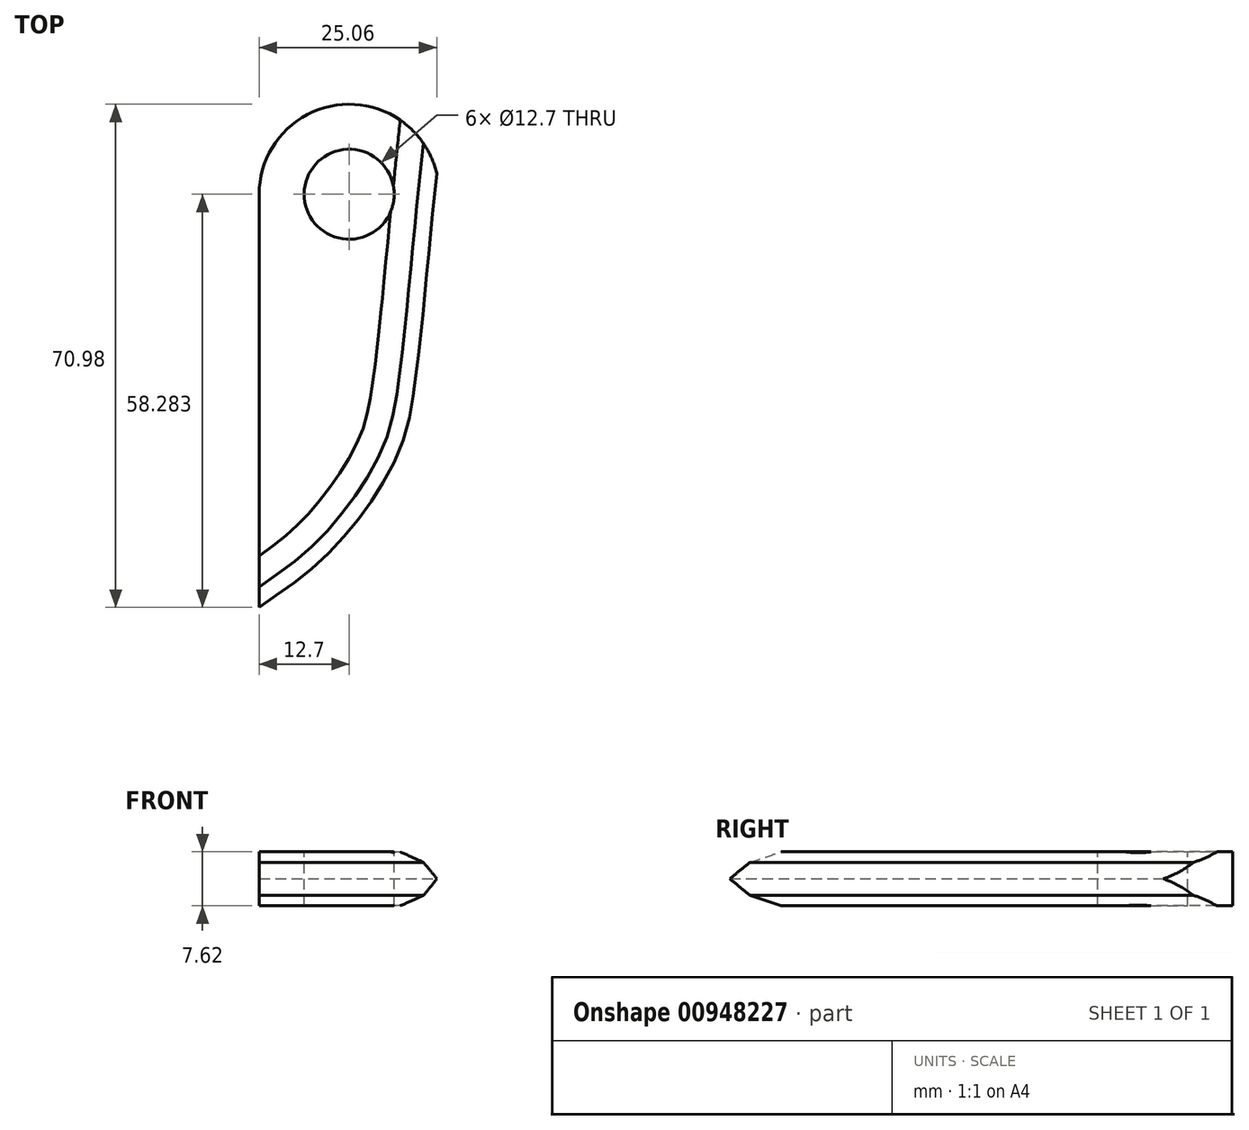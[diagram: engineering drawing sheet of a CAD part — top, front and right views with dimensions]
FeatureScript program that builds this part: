
annotation { "Feature Type Name" : "Feature", "Feature Type Description" : "" }
export const myFeature = defineFeature(function(context is Context, id is Id, definition is map)
    precondition{}
    {
        {
            var Q0;
            Q0=qCreatedBy(makeId("Top.planeOp"),FACE);
            var sketch = newSketch(context, id + "F0", { "sketchPlane" : qUnion([Q0])});
            skFitSpline(sketch, "E0", {"points": [v(-12.7, -23.04) * mm, v(-2.33, -14.95) * mm, v(6.74, -2.45) * mm, v(9.68, 7.6) * mm, v(12.7, 36.02) * mm], "startDerivative": vector(46.26, 33.05) * mm, "endDerivative": vector(9.99, 96.34) * mm});
            skLineSegment(sketch, "E1", {"start": v(-12.7, 36.02) * mm, "end": v(-12.7, -23.04) * mm});
            skArc(sketch, "E2", {"start": v(12.7, 36.02) * mm, "mid": v(0, 48.72) * mm, "end": v(-12.7, 36.02) * mm});
            skSolve(sketch);
        }
        {
            var Q0;
            Q0=makeQuery(id+"F0.imprint","IMPRINT",FACE,{"disambiguationData":[TD([[makeQuery(id+"F0.imprint","IMPRINT",EDGE,{"derivedFrom":sQuery(id+"F0.wireOp",EDGE,"E0")}),1.0]])]});
            extrude(context, id + "F1", {"entities" : qUnion([Q0]), "depth" : 7.62 * mm, "offsetDistance" : 25.4 * mm});
        }
        {
            var Q0;
            Q0=makeQuery(id+"F1.opExtrude","CAP_FACE",FACE,{"disambiguationData":[OSD([sQuery(id+"F0.wireOp",EDGE,"E0"),sQuery(id+"F0.wireOp",EDGE,"E1"),sQuery(id+"F0.wireOp",EDGE,"E2")])],"isStart":false});
            var sketch = newSketch(context, id + "F2", { "sketchPlane" : qUnion([Q0])});
            skCircle(sketch, "E3", {"center": v(0, 36.02) * mm, "radius": 6.35 * mm});
            skSolve(sketch);
        }
        {
            var Q0;
            Q0=makeQuery(id+"F2.imprint","IMPRINT",FACE,{"disambiguationData":[TD([[makeQuery(id+"F2.imprint","IMPRINT",EDGE,{"derivedFrom":sQuery(id+"F2.wireOp",EDGE,"E3")}),1.0]])]});
            extrude(context, id + "F3", {"entities" : qUnion([Q0]), "operationType" : NewBodyOperationType.REMOVE, "oppositeDirection" : true, "depth" : 25.4 * mm, "offsetDistance" : 25.4 * mm});
        }
        {
            var Q0;
            Q0=makeQuery(id+"F1.opExtrude","CAP_EDGE",EDGE,{"disambiguationData":[OSD([sQuery(id+"F0.wireOp",EDGE,"E0")])],"isStart":false});
            chamfer(context, id + "F4", {"entities" : qUnion([Q0]), "width" : 4.44 * mm, "tangentPropagation" : true});
        }
        {
            var Q0;
            Q0=makeQuery(id+"F1.opExtrude","CAP_EDGE",EDGE,{"disambiguationData":[OSD([sQuery(id+"F0.wireOp",EDGE,"E0")])],"isStart":true});
            chamfer(context, id + "F5", {"entities" : qUnion([Q0]), "width" : 4.44 * mm, "tangentPropagation" : true});
        }
        {
            var Q0;
            {var subQ0=sQuery(id+"F0.wireOp",EDGE,"E0");Q0=makeQuery(id+"F4.opChamfer","BLEND_EDGE",EDGE,{"blendedFrom":[makeQuery(id+"F1.opExtrude","CAP_EDGE",EDGE,{"disambiguationData":[OSD([subQ0])],"isStart":false}),makeQuery(id+"F1.opExtrude","CAP_FACE",FACE,{"disambiguationData":[OSD([subQ0,sQuery(id+"F0.wireOp",EDGE,"E1"),sQuery(id+"F0.wireOp",EDGE,"E2")])],"isStart":false})],"blendedInto":[makeQuery(id+"F1.opExtrude","CAP_FACE",FACE,{"disambiguationData":[OSD([subQ0,sQuery(id+"F0.wireOp",EDGE,"E1"),sQuery(id+"F0.wireOp",EDGE,"E2")])],"isStart":false})]});}
            chamfer(context, id + "F6", {"entities" : qUnion([Q0]), "width" : 5.08 * mm, "tangentPropagation" : true});
        }
        {
            var Q0;
            {var subQ0=sQuery(id+"F0.wireOp",EDGE,"E0");Q0=makeQuery(id+"F5.opChamfer","BLEND_EDGE",EDGE,{"blendedFrom":[makeQuery(id+"F1.opExtrude","CAP_EDGE",EDGE,{"disambiguationData":[OSD([subQ0])],"isStart":true}),makeQuery(id+"F1.opExtrude","CAP_FACE",FACE,{"disambiguationData":[OSD([subQ0,sQuery(id+"F0.wireOp",EDGE,"E1"),sQuery(id+"F0.wireOp",EDGE,"E2")])],"isStart":true})],"blendedInto":[makeQuery(id+"F1.opExtrude","CAP_FACE",FACE,{"disambiguationData":[OSD([subQ0,sQuery(id+"F0.wireOp",EDGE,"E1"),sQuery(id+"F0.wireOp",EDGE,"E2")])],"isStart":true})]});}
            chamfer(context, id + "F7", {"entities" : qUnion([Q0]), "width" : 5.08 * mm, "tangentPropagation" : true});
        }
    });
